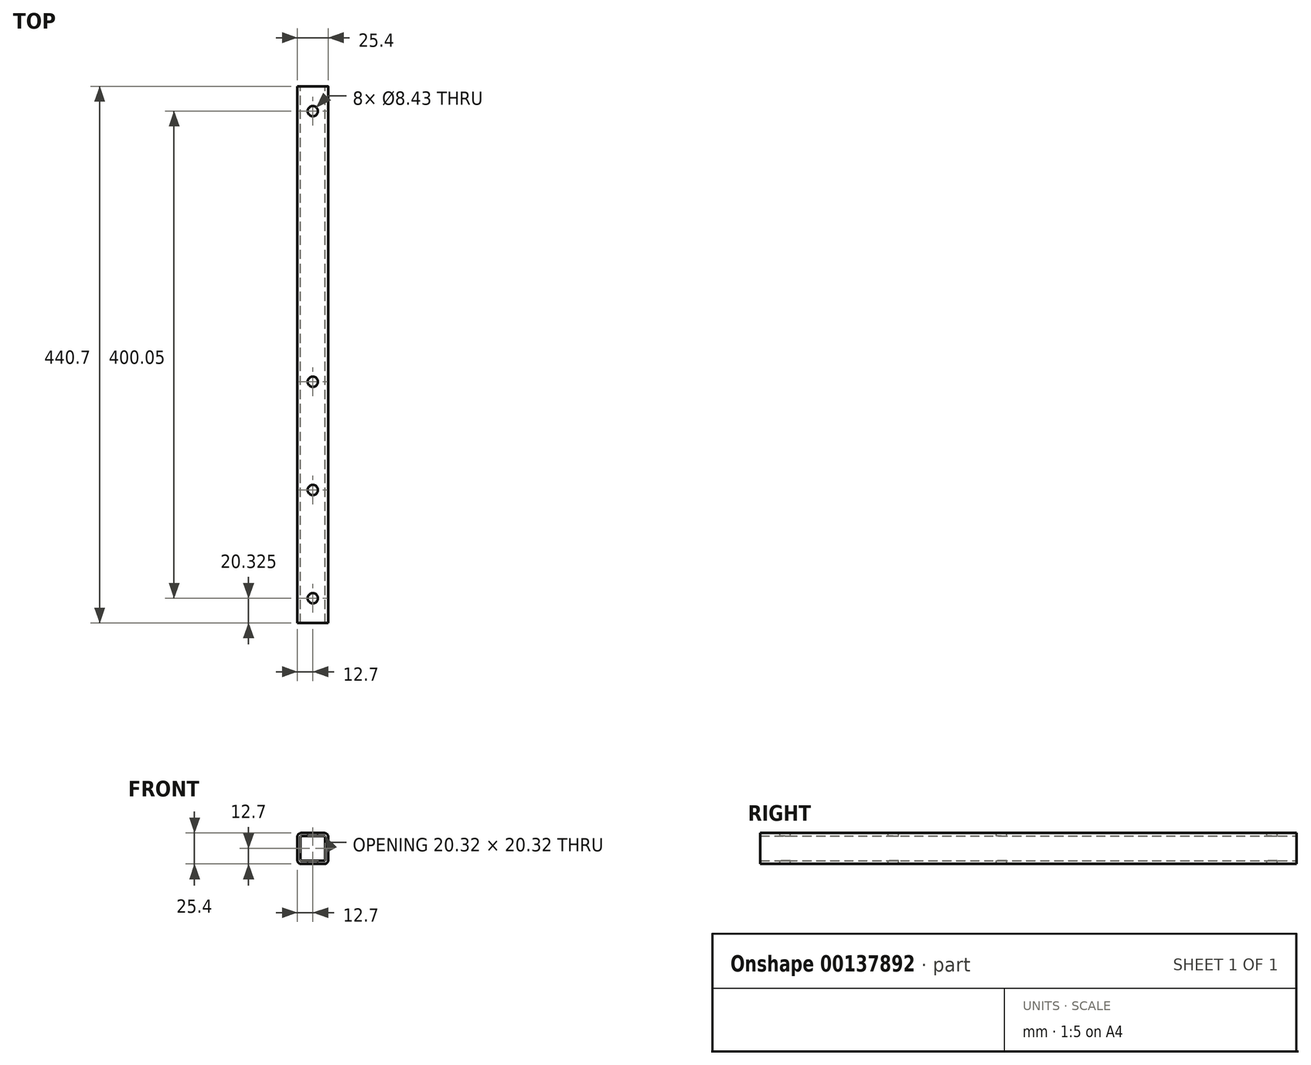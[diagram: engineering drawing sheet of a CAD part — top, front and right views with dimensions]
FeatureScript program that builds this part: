
annotation { "Feature Type Name" : "Feature", "Feature Type Description" : "" }
export const myFeature = defineFeature(function(context is Context, id is Id, definition is map)
    precondition{}
    {
        {
            var Q0;
            Q0=qCreatedBy(makeId("Front.planeOp"),FACE);
            var sketch = newSketch(context, id + "F0", { "sketchPlane" : qUnion([Q0])});
            skLineSegment(sketch, "E0.bottom", {"start": v(12.7, 12.7) * mm, "end": v(-12.7, 12.7) * mm});
            skLineSegment(sketch, "E0.top", {"start": v(12.7, -12.7) * mm, "end": v(-12.7, -12.7) * mm});
            skLineSegment(sketch, "E0.left", {"start": v(12.7, 12.7) * mm, "end": v(12.7, -12.7) * mm});
            skLineSegment(sketch, "E0.right", {"start": v(-12.7, 12.7) * mm, "end": v(-12.7, -12.7) * mm});
            skPoint(sketch, "E0.middle", {"position": v(0, 0) * mm});
            skSolve(sketch);
        }
        {
            var Q0;
            Q0 = qSketchRegion(id + "F0", true);
            extrude(context, id + "F1", {"entities" : qUnion([Q0]), "endBound" : BoundingType.SYMMETRIC, "depth" : 440.7 * mm});
        }
        {
            var Q0;
            Q0=makeQuery(id+"F1.opExtrude","SWEPT_EDGE",EDGE,{"disambiguationData":[OSD([sQuery(id+"F0.wireOp",EDGE,"E0.bottom"),sQuery(id+"F0.wireOp",EDGE,"E0.right")])]});
            var Q1;
            Q1=makeQuery(id+"F1.opExtrude","SWEPT_EDGE",EDGE,{"disambiguationData":[OSD([sQuery(id+"F0.wireOp",EDGE,"E0.bottom"),sQuery(id+"F0.wireOp",EDGE,"E0.left")])]});
            var Q2;
            Q2=makeQuery(id+"F1.opExtrude","SWEPT_EDGE",EDGE,{"disambiguationData":[OSD([sQuery(id+"F0.wireOp",EDGE,"E0.top"),sQuery(id+"F0.wireOp",EDGE,"E0.right")])]});
            var Q3;
            Q3=makeQuery(id+"F1.opExtrude","SWEPT_EDGE",EDGE,{"disambiguationData":[OSD([sQuery(id+"F0.wireOp",EDGE,"E0.top"),sQuery(id+"F0.wireOp",EDGE,"E0.left")])]});
            fillet(context, id + "F2", {"entities" : qUnion([Q0, Q1, Q2, Q3]), "radius" : 3.17 * mm, "tangentPropagation" : true, "allowEdgeOverflow" : false});
        }
        {
            var Q0;
            Q0=makeQuery(id+"F1.opExtrude","CAP_FACE",FACE,{"disambiguationData":[OSD([sQuery(id+"F0.wireOp",EDGE,"E0.bottom"),sQuery(id+"F0.wireOp",EDGE,"E0.top"),sQuery(id+"F0.wireOp",EDGE,"E0.left"),sQuery(id+"F0.wireOp",EDGE,"E0.right")])],"isStart":false});
            var Q1;
            Q1=makeQuery(id+"F1.opExtrude","CAP_FACE",FACE,{"disambiguationData":[OSD([sQuery(id+"F0.wireOp",EDGE,"E0.bottom"),sQuery(id+"F0.wireOp",EDGE,"E0.top"),sQuery(id+"F0.wireOp",EDGE,"E0.left"),sQuery(id+"F0.wireOp",EDGE,"E0.right")])],"isStart":true});
            shell(context, id + "F3", {"entities" : qUnion([Q0, Q1]), "thickness" : 2.54 * mm});
        }
        {
            var Q0;
            Q0=makeQuery(id+"F1.opExtrude","SWEPT_FACE",FACE,{"disambiguationData":[OSD([sQuery(id+"F0.wireOp",EDGE,"E0.bottom")])]});
            var sketch = newSketch(context, id + "F4", { "sketchPlane" : qUnion([Q0])});
            skPoint(sketch, "E1", {"position": v(0, -200.03) * mm});
            skPoint(sketch, "E2", {"position": v(0, -22.23) * mm});
            skPoint(sketch, "E3", {"position": v(0, 200.03) * mm});
            skPoint(sketch, "E3.positionSnap0", {"position": v(0, 220.35) * mm});
            skPoint(sketch, "E4", {"position": v(0, -111.13) * mm});
            skPoint(sketch, "E4.positionSnap0", {"position": v(0, -220.35) * mm});
            skLineSegment(sketch, "E5", {"start": v(0, -200.03) * mm, "end": v(0, -22.23) * mm, "construction": true});
            skSolve(sketch);
        }
        {
            var Q0;
            Q0=sQuery(id+"F4.wireOp",VERTEX,"E1");
            var Q1;
            Q1=sQuery(id+"F4.wireOp",VERTEX,"E2");
            var Q2;
            Q2=sQuery(id+"F4.wireOp",VERTEX,"E3");
            var Q3;
            Q3=sQuery(id+"F4.wireOp",VERTEX,"E4");
            var Q4;
            Q4=makeQuery(id+"F1.opExtrude","SWEPT_BODY",BODY,{"disambiguationData":[OSD([sQuery(id+"F0.wireOp",EDGE,"E0.bottom"),sQuery(id+"F0.wireOp",EDGE,"E0.top"),sQuery(id+"F0.wireOp",EDGE,"E0.left"),sQuery(id+"F0.wireOp",EDGE,"E0.right")])]});
            hole(context, id + "F5", {"style" : HoleStyle.SIMPLE, "endStyle" : HoleEndStyle.THROUGH, "standardTappedOrClearance" : lookupTablePath({ "standard" : "ANSI", "fit" : "Normal (ASME)", "size" : "5/16", "type" : "Clearance" }), "standardBlindInLast" : lookupTablePath({ "fit" : "Free", "standard" : "ANSI", "size" : "5/16", "type" : "Clearance" }), "holeDiameter" : 8.43 * mm, "locations" : qUnion([Q0, Q1, Q2, Q3]), "scope" : qUnion([Q4]), "isTappedThrough" : true});
        }
    });
